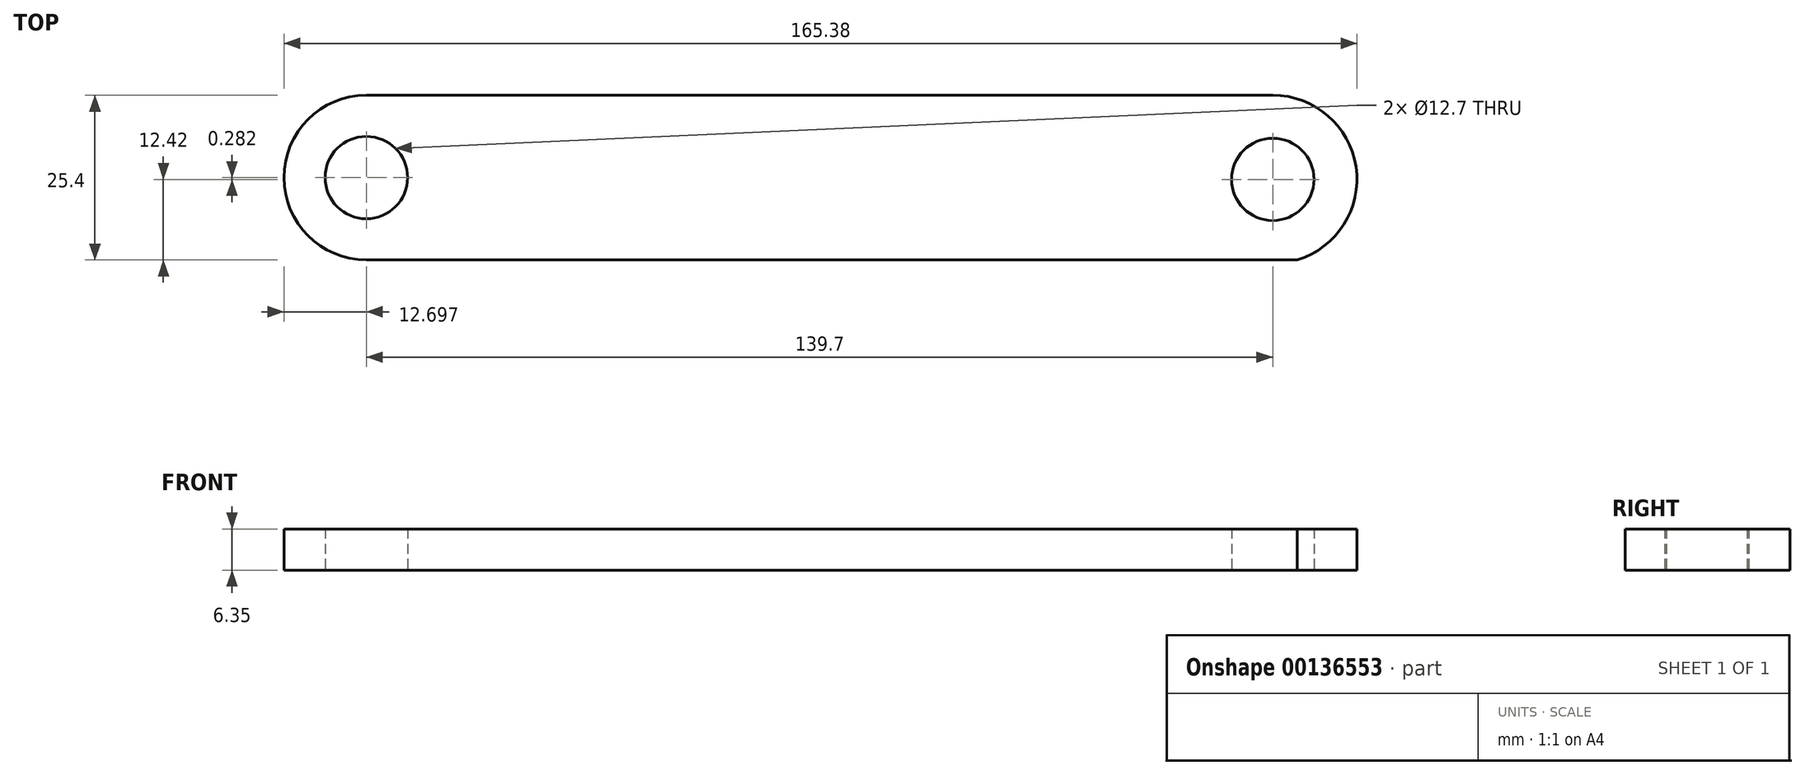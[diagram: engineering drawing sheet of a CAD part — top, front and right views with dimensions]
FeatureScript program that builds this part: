
annotation { "Feature Type Name" : "Feature", "Feature Type Description" : "" }
export const myFeature = defineFeature(function(context is Context, id is Id, definition is map)
    precondition{}
    {
        {
            var Q0;
            Q0=qCreatedBy(makeId("Top.planeOp"),FACE);
            var sketch = newSketch(context, id + "F0", { "sketchPlane" : qUnion([Q0])});
            skLineSegment(sketch, "E0", {"start": v(-74.36, 8.27) * mm, "end": v(65.34, 8.27) * mm});
            skLineSegment(sketch, "E1", {"start": v(-74.36, -17.13) * mm, "end": v(69.12, -17.13) * mm});
            skArc(sketch, "E2", {"start": v(69.12, -17.13) * mm, "mid": v(78.18, -2.8) * mm, "end": v(65.34, 8.27) * mm});
            skArc(sketch, "E3", {"start": v(-74.36, 8.27) * mm, "mid": v(-87.06, -4.43) * mm, "end": v(-74.36, -17.13) * mm});
            skCircle(sketch, "E4", {"center": v(65.34, -4.7) * mm, "radius": 6.35 * mm});
            skCircle(sketch, "E5", {"center": v(-74.36, -4.43) * mm, "radius": 6.35 * mm});
            skSolve(sketch);
        }
        {
            var Q0;
            Q0=makeQuery(id+"F0.imprint","IMPRINT",FACE,{"disambiguationData":[TD([[makeQuery(id+"F0.imprint","IMPRINT",EDGE,{"derivedFrom":sQuery(id+"F0.wireOp",EDGE,"E0")}),-1.0]])]});
            extrude(context, id + "F1", {"entities" : qUnion([Q0]), "depth" : 6.35 * mm});
        }
    });
